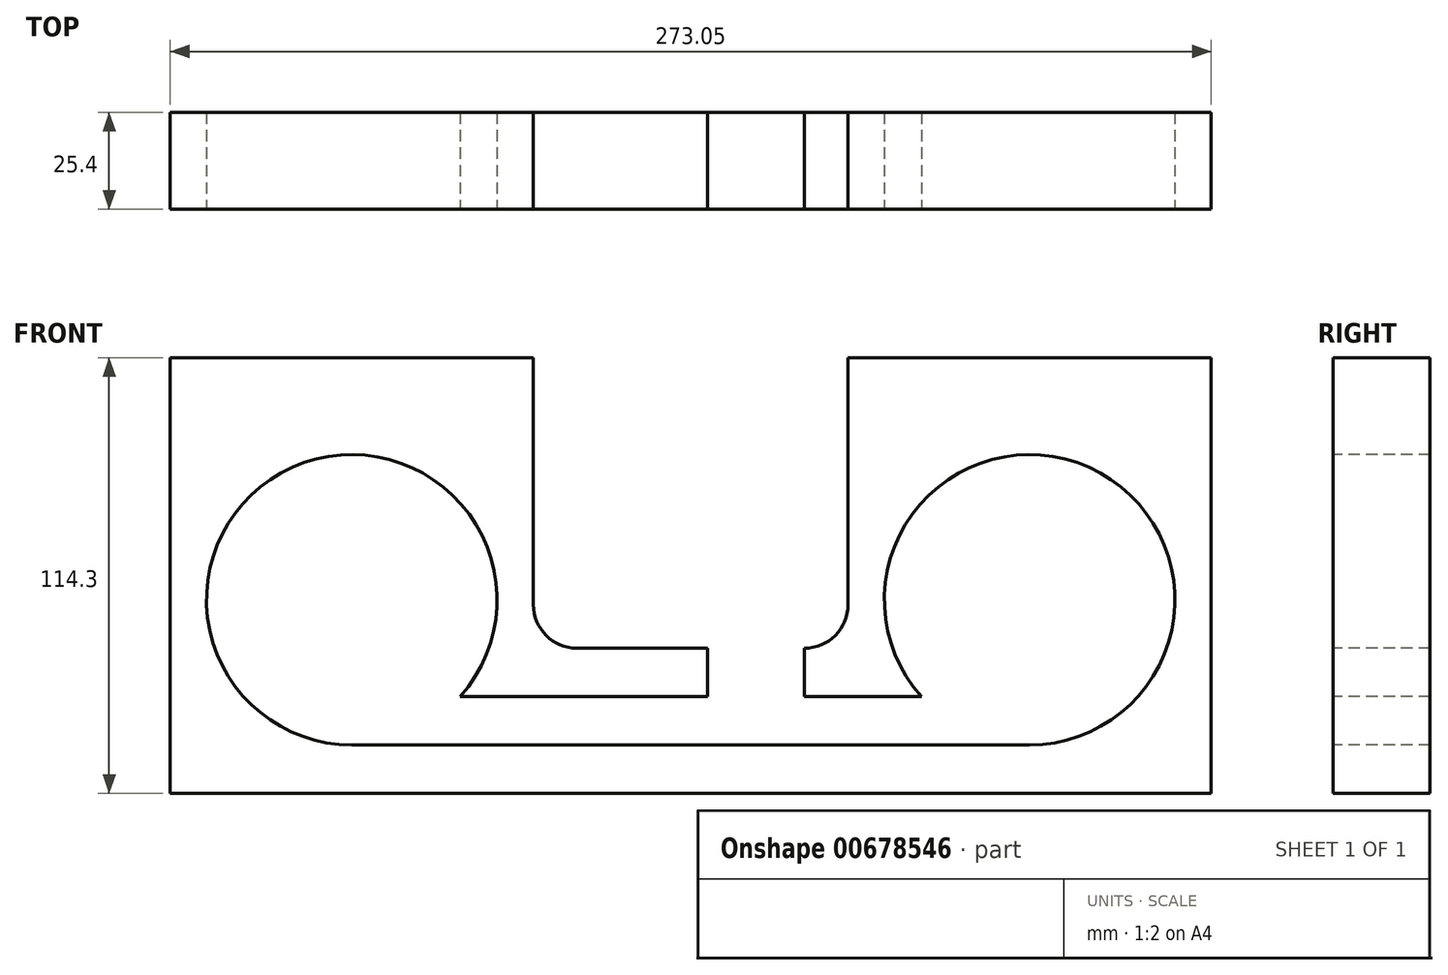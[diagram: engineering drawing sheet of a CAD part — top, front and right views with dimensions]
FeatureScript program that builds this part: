
annotation { "Feature Type Name" : "Feature", "Feature Type Description" : "" }
export const myFeature = defineFeature(function(context is Context, id is Id, definition is map)
    precondition{}
    {
        {
            var Q0;
            Q0=qCreatedBy(makeId("Front.planeOp"),FACE);
            var sketch = newSketch(context, id + "F0", { "sketchPlane" : qUnion([Q0])});
            skLineSegment(sketch, "E0.bottom", {"start": v(0, 0) * mm, "end": v(273.05, 0) * mm});
            skLineSegment(sketch, "E0.top", {"start": v(0, 114.3) * mm, "end": v(273.05, 114.3) * mm});
            skLineSegment(sketch, "E0.left", {"start": v(0, 0) * mm, "end": v(0, 114.3) * mm});
            skLineSegment(sketch, "E0.right", {"start": v(273.05, 0) * mm, "end": v(273.05, 114.3) * mm});
            skSolve(sketch);
        }
        {
            var Q0;
            Q0=makeQuery(id+"F0.imprint","IMPRINT",FACE,{"disambiguationData":[TD([[makeQuery(id+"F0.imprint","IMPRINT",EDGE,{"derivedFrom":sQuery(id+"F0.wireOp",EDGE,"E0.bottom")}),1.0]])]});
            extrude(context, id + "F1", {"entities" : qUnion([Q0]), "depth" : 25.4 * mm, "offsetDistance" : 25.4 * mm});
        }
        {
            var Q0;
            Q0=makeQuery(id+"F1.opExtrude","CAP_FACE",FACE,{"disambiguationData":[OSD([sQuery(id+"F0.wireOp",EDGE,"E0.bottom"),sQuery(id+"F0.wireOp",EDGE,"E0.top"),sQuery(id+"F0.wireOp",EDGE,"E0.left"),sQuery(id+"F0.wireOp",EDGE,"E0.right")])],"isStart":false});
            var sketch = newSketch(context, id + "F2", { "sketchPlane" : qUnion([Q0])});
            skCircle(sketch, "E1", {"center": v(47.62, 50.8) * mm, "radius": 38.1 * mm});
            skCircle(sketch, "E2", {"center": v(225.43, 50.8) * mm, "radius": 38.1 * mm});
            skSolve(sketch);
        }
        {
            var Q0;
            Q0=makeQuery(id+"F2.imprint","IMPRINT",FACE,{"disambiguationData":[TD([[makeQuery(id+"F2.imprint","IMPRINT",EDGE,{"derivedFrom":sQuery(id+"F2.wireOp",EDGE,"E1")}),1.0]])]});
            var Q1;
            Q1=makeQuery(id+"F2.imprint","IMPRINT",FACE,{"disambiguationData":[TD([[makeQuery(id+"F2.imprint","IMPRINT",EDGE,{"derivedFrom":sQuery(id+"F2.wireOp",EDGE,"E2")}),1.0]])]});
            extrude(context, id + "F3", {"entities" : qUnion([Q0, Q1]), "operationType" : NewBodyOperationType.REMOVE, "oppositeDirection" : true, "depth" : 25.4 * mm, "offsetDistance" : 25.4 * mm});
        }
        {
            var Q0;
            Q0=makeQuery(id+"F1.opExtrude","CAP_FACE",FACE,{"disambiguationData":[OSD([sQuery(id+"F0.wireOp",EDGE,"E0.bottom"),sQuery(id+"F0.wireOp",EDGE,"E0.top"),sQuery(id+"F0.wireOp",EDGE,"E0.left"),sQuery(id+"F0.wireOp",EDGE,"E0.right")])],"isStart":false});
            var sketch = newSketch(context, id + "F4", { "sketchPlane" : qUnion([Q0])});
            skLineSegment(sketch, "E3.bottom", {"start": v(95.25, 114.3) * mm, "end": v(177.8, 114.3) * mm});
            skLineSegment(sketch, "E3.top", {"start": v(106.68, 38.1) * mm, "end": v(166.37, 38.1) * mm});
            skLineSegment(sketch, "E3.left", {"start": v(95.25, 114.3) * mm, "end": v(95.25, 49.53) * mm});
            skLineSegment(sketch, "E3.right", {"start": v(177.8, 114.3) * mm, "end": v(177.8, 49.53) * mm});
            skPoint(sketch, "E4.visualSharp", {"position": v(95.25, 38.1) * mm});
            skArc(sketch, "E4.filletArc", {"start": v(95.25, 49.53) * mm, "mid": v(98.6, 41.45) * mm, "end": v(106.68, 38.1) * mm});
            skPoint(sketch, "E5.visualSharp", {"position": v(177.8, 38.1) * mm});
            skArc(sketch, "E5.filletArc", {"start": v(166.37, 38.1) * mm, "mid": v(174.45, 41.45) * mm, "end": v(177.8, 49.53) * mm});
            skLineSegment(sketch, "E6", {"start": v(177.8, 114.3) * mm, "end": v(273.05, 114.3) * mm});
            skSolve(sketch);
        }
        {
            var Q0;
            Q0=makeQuery(id+"F4.imprint","IMPRINT",FACE,{"disambiguationData":[TD([[makeQuery(id+"F4.imprint","IMPRINT",EDGE,{"derivedFrom":sQuery(id+"F4.wireOp",EDGE,"E3.bottom")}),-1.0]])]});
            extrude(context, id + "F5", {"entities" : qUnion([Q0]), "operationType" : NewBodyOperationType.REMOVE, "oppositeDirection" : true, "depth" : 25.4 * mm, "offsetDistance" : 25.4 * mm});
        }
        {
            var Q0;
            Q0=makeQuery(id+"F1.opExtrude","CAP_FACE",FACE,{"disambiguationData":[OSD([sQuery(id+"F0.wireOp",EDGE,"E0.bottom"),sQuery(id+"F0.wireOp",EDGE,"E0.top"),sQuery(id+"F0.wireOp",EDGE,"E0.left"),sQuery(id+"F0.wireOp",EDGE,"E0.right")])],"isStart":false});
            var sketch = newSketch(context, id + "F6", { "sketchPlane" : qUnion([Q0])});
            skLineSegment(sketch, "E7", {"start": v(166.37, 38.1) * mm, "end": v(140.97, 38.1) * mm});
            skLineSegment(sketch, "E8", {"start": v(140.97, 38.1) * mm, "end": v(140.97, 25.4) * mm});
            skLineSegment(sketch, "E9", {"start": v(47.62, 12.7) * mm, "end": v(225.43, 12.7) * mm});
            skLineSegment(sketch, "E10", {"start": v(166.37, 38.1) * mm, "end": v(166.37, 25.4) * mm});
            skLineSegment(sketch, "E11", {"start": v(166.37, 25.4) * mm, "end": v(197.03, 25.4) * mm});
            skLineSegment(sketch, "E12", {"start": v(197.03, 25.4) * mm, "end": v(225.43, 12.7) * mm});
            skLineSegment(sketch, "E13", {"start": v(140.97, 25.4) * mm, "end": v(76.02, 25.4) * mm});
            skLineSegment(sketch, "E14", {"start": v(76.02, 25.4) * mm, "end": v(47.62, 12.7) * mm});
            skLineSegment(sketch, "E15", {"start": v(166.37, 25.4) * mm, "end": v(166.37, 12.7) * mm});
            skLineSegment(sketch, "E16", {"start": v(166.37, 12.7) * mm, "end": v(225.43, 12.7) * mm});
            skSolve(sketch);
        }
        {
            var Q0;
            Q0 = qSketchRegion(id + "F6", true);
            extrude(context, id + "F7", {"entities" : qUnion([Q0]), "operationType" : NewBodyOperationType.REMOVE, "oppositeDirection" : true, "depth" : 25.4 * mm, "offsetDistance" : 25.4 * mm});
        }
    });
